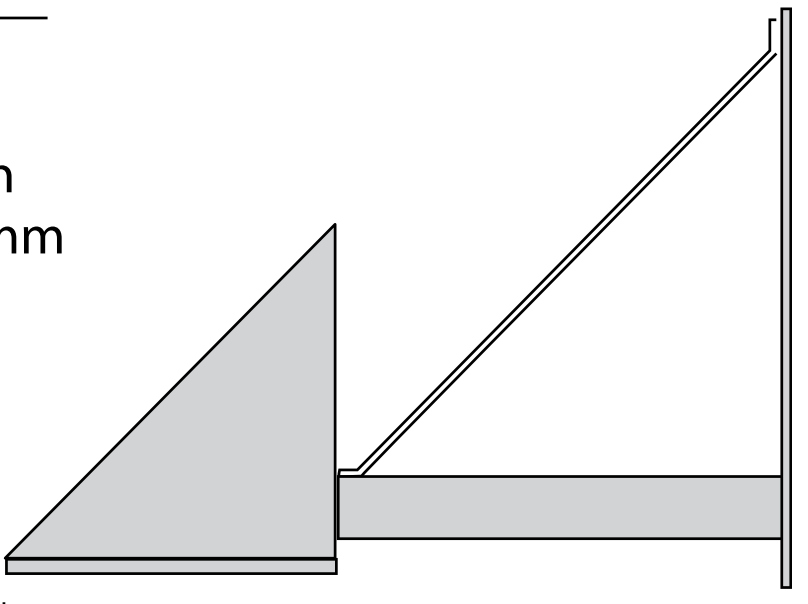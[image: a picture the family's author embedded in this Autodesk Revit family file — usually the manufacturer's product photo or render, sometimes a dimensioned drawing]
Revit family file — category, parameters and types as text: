
# Revit family: M2WDXA
name_source: partatom
category: Lighting Fixtures
revit_build: Autodesk Revit Architecture 2012 (Build: 20110309_2315(x64)
units: mm (PartAtom-declared; Revit-internal decimal feet)

## types (21) — shared parameters
Apparent Load = 0 VA
Color Filter = 16777215
Default Elevation = 48 "
Description = Horizontal reflector downlight with extended arm
Dimming Lamp Color Temperature Shift = <None>
Finish = Die Cast Aluminium
Finish 2 = Silicon Gasket
Glass = Glass
Lamp = One
Manufacturer = Architectural Area Lighting
Manufacturer Fax = 626-369-2695
Model = M2WDXA
Product Documentation Link = http://www.aal.net
Product Page URL = http://www.aal.net
Tilt Angle = 90.00°
URL = http://www.aal.net
Wattage Comments = 57 and 70 watts High Output Fluorescent

## per-type parameters (varying)
| type | Photometric Web File |
| M2WDXA-T2-32LED-3K-700 | M2-T2-32LED-3K-700.ies |
| M2WDXA-T3-32LED-3K-700 | M2-T3-32LED-3K-700.ies |
| M2WDXA-T4-32LED-3K-700 | M2-T4-32LED-3K-700.ies |
| M2WDXA-T4-32LED-3K-HSS-700 | M2-T4-32LED-3K-HSS-700.ies |
| M2WDXA-T5-32LED-3K-700 | M2-T5-32LED-3K-700.ies |
| M2WDXA-TL-32LED-3K-700 | M2-TL-32LED-3K-700.ies |
| M2WDXA-TR-32LED-3K-700 | M2-TR-32LED-3K-700.ies |
| M2WDXA-T2-32LED-4K-700 | M2-T2-32LED-4K-700.ies |
| M2WDXA-T3-32LED-4K-700 | M2-T3-32LED-4K-700.ies |
| M2WDXA-T4-32LED-4K-700 | M2-T4-32LED-4K-700.ies |
| M2WDXA-T4-32LED-4K-HSS-700 | M2-T4-32LED-4K-HSS-700.ies |
| M2WDXA-T5-32LED-4K-700 | M2-T5-32LED-4K-700.ies |
| M2WDXA-TL-32LED-4K-700 | M2-TL-32LED-4K-700.ies |
| M2WDXA-T2-32LED-5K-700 | M2-T2-32LED-5K-700.ies |
| M2WDXA-T2-32LED-5K-HSS-700 | M2-T2-32LED-5K-HSS-700.ies |
| M2WDXA-T3-32LED-5K-700 | M2-T3-32LED-5K-700.ies |
| M2WDXA-T4-32LED-5K-700 | M2-T4-32LED-5K-700.ies |
| M2WDXA-T4-32LED-5K-HSS-700 | M2-T4-32LED-5K-HSS-700.ies |
| M2WDXA-T5-32LED-5K-700 | M2-T5-32LED-5K-700.ies |
| M2WDXA-TL-32LED-5K-700 | M2-TL-32LED-5K-700.ies |
| M2WDXA-TR-32LED-5K-700 | M2-TR-32LED-5K-700.ies |

## geometry (parser evidence)
native form markers: Blend x4, Sweep x5
no freeform markers — native parametric forms only
